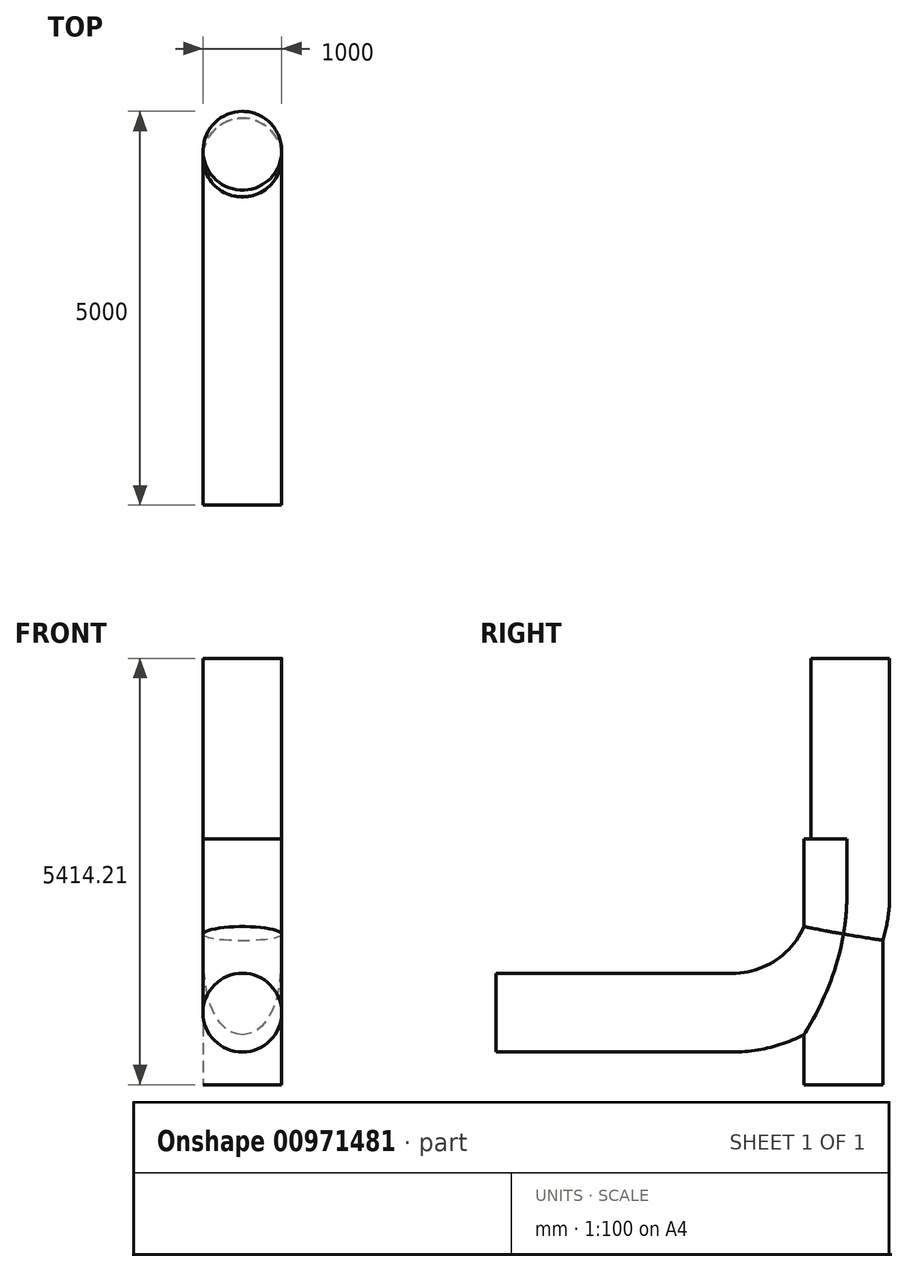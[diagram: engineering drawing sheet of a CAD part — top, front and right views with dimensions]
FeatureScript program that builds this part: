
annotation { "Feature Type Name" : "Feature", "Feature Type Description" : "" }
export const myFeature = defineFeature(function(context is Context, id is Id, definition is map)
    precondition{}
    {
        {
            var Q0;
            Q0=qCreatedBy(makeId("Front.planeOp"),FACE);
            var sketch = newSketch(context, id + "F0", { "sketchPlane" : qUnion([Q0])});
            skCircle(sketch, "E0", {"center": v(0, 0) * mm, "radius": 500 * mm});
            skSolve(sketch);
        }
        {
            var Q0;
            Q0=qCreatedBy(makeId("Right.planeOp"),FACE);
            var sketch = newSketch(context, id + "F1", { "sketchPlane" : qUnion([Q0])});
            skLineSegment(sketch, "E1", {"start": v(0, 0) * mm, "end": v(3000, 0) * mm});
            skLineSegment(sketch, "E2", {"start": v(4500, 1500) * mm, "end": v(4500, 4500) * mm});
            skArc(sketch, "E3", {"start": v(4500, 1500) * mm, "mid": v(4060.66, 439.34) * mm, "end": v(3000, 0) * mm});
            skLineSegment(sketch, "E4", {"start": v(3000, 1500) * mm, "end": v(4500, 1500) * mm});
            skLineSegment(sketch, "E5", {"start": v(3000, 1500) * mm, "end": v(4827.04, -327.04) * mm});
            skArc(sketch, "E6.0", {"start": v(5000, 1500) * mm, "mid": v(4414.21, 85.79) * mm, "end": v(3000, -500) * mm});
            skLineSegment(sketch, "E7", {"start": v(4414.21, 85.79) * mm, "end": v(4414.21, -914.21) * mm});
            skSolve(sketch);
        }
        {
            var Q0;
            Q0=makeQuery(id+"F0.imprint","IMPRINT",FACE,{"disambiguationData":[TD([[makeQuery(id+"F0.imprint","IMPRINT",EDGE,{"derivedFrom":sQuery(id+"F0.wireOp",EDGE,"E0")}),1.0]])]});
            var Q1;
            Q1=sQuery(id+"F1.wireOp",EDGE,"E1");
            var Q2;
            Q2=sQuery(id+"F1.wireOp",EDGE,"E3");
            var Q3;
            Q3=sQuery(id+"F1.wireOp",EDGE,"E2");
            sweep(context, id + "F2", {"profiles" : qUnion([Q0]), "path" : qUnion([Q1, Q2, Q3])});
        }
        {
            var Q0;
            Q0=sQuery(id+"F1.wireOp",VERTEX,"E7.end");
            var Q1;
            Q1=sQuery(id+"F1.wireOp",EDGE,"E7");
            cPlane(context, id + "F3", {"entities" : qUnion([Q0, Q1]), "cplaneType" : CPlaneType.LINE_POINT, "offset" : 25 * mm, "width" : 150 * mm, "height" : 150 * mm});
        }
        {
            var Q0;
            Q0=qCreatedBy(id+"F3.planeOp",FACE);
            var sketch = newSketch(context, id + "F4", { "sketchPlane" : qUnion([Q0])});
            skPoint(sketch, "E8", {"position": v(0, -67320.9) * mm});
            skCircle(sketch, "E9", {"center": v(0, -67320.9) * mm, "radius": 500 * mm});
            skCircle(sketch, "E10", {"center": v(0, -4414.03) * mm, "radius": 500 * mm});
            skSolve(sketch);
        }
        {
            var Q0;
            Q0=makeQuery(id+"F4.imprint","IMPRINT",FACE,{"disambiguationData":[TD([[makeQuery(id+"F4.imprint","IMPRINT",EDGE,{"derivedFrom":sQuery(id+"F4.wireOp",EDGE,"E10")}),1.0]])]});
            extrude(context, id + "F5", {"entities" : qUnion([Q0]), "operationType" : NewBodyOperationType.ADD, "oppositeDirection" : true, "depth" : 3120 * mm, "offsetDistance" : 25 * mm});
        }
    });
